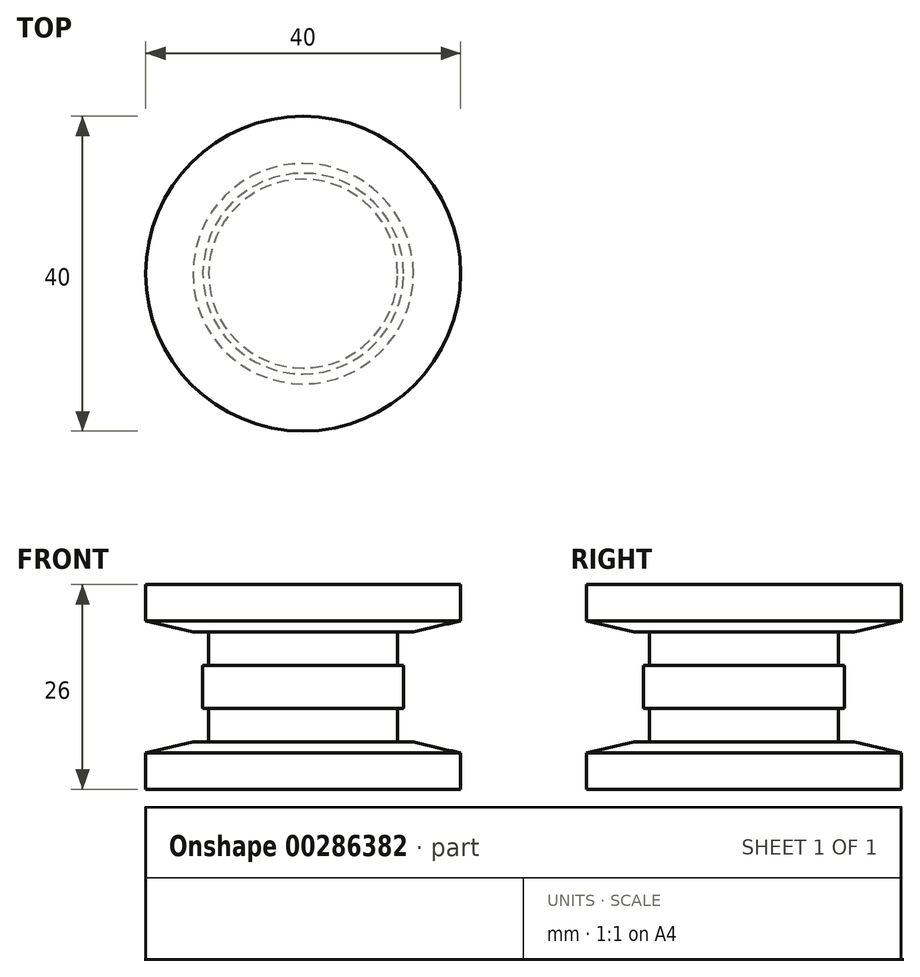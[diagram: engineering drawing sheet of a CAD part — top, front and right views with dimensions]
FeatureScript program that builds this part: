
annotation { "Feature Type Name" : "Feature", "Feature Type Description" : "" }
export const myFeature = defineFeature(function(context is Context, id is Id, definition is map)
    precondition{}
    {
        {
            var Q0;
            Q0=qCreatedBy(makeId("Top.planeOp"),FACE);
            var sketch = newSketch(context, id + "F0", { "sketchPlane" : qUnion([Q0])});
            skCircle(sketch, "E0", {"center": v(0, 0) * mm, "radius": 20 * mm});
            skSolve(sketch);
        }
        {
            var Q0;
            Q0 = qSketchRegion(id + "F0", true);
            extrude(context, id + "F1", {"entities" : qUnion([Q0]), "depth" : 6 * mm});
        }
        {
            var Q0;
            Q0=makeQuery(id+"F1.opExtrude","CAP_FACE",FACE,{"disambiguationData":[OSD([sQuery(id+"F0.wireOp",EDGE,"E0")])],"isStart":false});
            cPlane(context, id + "F2", {"entities" : qUnion([Q0]), "cplaneType" : CPlaneType.OFFSET, "offset" : 0 * mm, "width" : 150 * mm, "height" : 150 * mm});
        }
        {
            var Q0;
            Q0=qCreatedBy(id+"F2.planeOp",FACE);
            var sketch = newSketch(context, id + "F3", { "sketchPlane" : qUnion([Q0])});
            skCircle(sketch, "E1", {"center": v(0, 0) * mm, "radius": 12 * mm});
            skSolve(sketch);
        }
        {
            var Q0;
            Q0 = qSketchRegion(id + "F3", true);
            extrude(context, id + "F4", {"entities" : qUnion([Q0]), "operationType" : NewBodyOperationType.ADD, "depth" : 4.25 * mm});
        }
        {
            var Q0;
            Q0=makeQuery(id+"F4.opExtrude","CAP_FACE",FACE,{"disambiguationData":[OSD([sQuery(id+"F3.wireOp",EDGE,"E1")])],"isStart":false});
            cPlane(context, id + "F5", {"entities" : qUnion([Q0]), "cplaneType" : CPlaneType.OFFSET, "offset" : 0 * mm, "width" : 150 * mm, "height" : 150 * mm});
        }
        {
            var Q0;
            Q0=qCreatedBy(id+"F5.planeOp",FACE);
            var sketch = newSketch(context, id + "F6", { "sketchPlane" : qUnion([Q0])});
            skCircle(sketch, "E2", {"center": v(0, 0) * mm, "radius": 12.75 * mm});
            skSolve(sketch);
        }
        {
            var Q0;
            Q0 = qSketchRegion(id + "F6", true);
            extrude(context, id + "F7", {"entities" : qUnion([Q0]), "operationType" : NewBodyOperationType.ADD, "depth" : 5.5 * mm});
        }
        {
            var Q0;
            Q0=makeQuery(id+"F7.opExtrude","CAP_FACE",FACE,{"disambiguationData":[OSD([sQuery(id+"F6.wireOp",EDGE,"E2")])],"isStart":false});
            cPlane(context, id + "F8", {"entities" : qUnion([Q0]), "cplaneType" : CPlaneType.OFFSET, "offset" : 0 * mm, "width" : 150 * mm, "height" : 150 * mm});
        }
        {
            var Q0;
            Q0=qCreatedBy(id+"F8.planeOp",FACE);
            var sketch = newSketch(context, id + "F9", { "sketchPlane" : qUnion([Q0])});
            skCircle(sketch, "E3", {"center": v(0, 0) * mm, "radius": 12 * mm});
            skSolve(sketch);
        }
        {
            var Q0;
            Q0 = qSketchRegion(id + "F9", true);
            extrude(context, id + "F10", {"entities" : qUnion([Q0]), "operationType" : NewBodyOperationType.ADD, "depth" : 4.25 * mm});
        }
        {
            var Q0;
            Q0=makeQuery(id+"F10.opExtrude","CAP_FACE",FACE,{"disambiguationData":[OSD([sQuery(id+"F9.wireOp",EDGE,"E3")])],"isStart":false});
            cPlane(context, id + "F11", {"entities" : qUnion([Q0]), "cplaneType" : CPlaneType.OFFSET, "offset" : 0 * mm, "width" : 150 * mm, "height" : 150 * mm});
        }
        {
            var Q0;
            Q0=qCreatedBy(id+"F11.planeOp",FACE);
            var sketch = newSketch(context, id + "F12", { "sketchPlane" : qUnion([Q0])});
            skCircle(sketch, "E4", {"center": v(0, 0) * mm, "radius": 20 * mm});
            skSolve(sketch);
        }
        {
            var Q0;
            Q0 = qSketchRegion(id + "F12", true);
            extrude(context, id + "F13", {"entities" : qUnion([Q0]), "operationType" : NewBodyOperationType.ADD, "depth" : 6 * mm});
        }
        {
            var Q0;
            Q0=makeQuery(id+"F1.opExtrude","CAP_EDGE",EDGE,{"disambiguationData":[OSD([sQuery(id+"F0.wireOp",EDGE,"E0")])],"isStart":false});
            chamfer(context, id + "F14", {"entities" : qUnion([Q0]), "chamferType" : ChamferType.TWO_OFFSETS, "width1" : 6 * mm, "oppositeDirection" : false, "width2" : 1.4 * mm, "tangentPropagation" : true});
        }
        {
            var Q0;
            Q0=makeQuery(id+"F13.opExtrude","CAP_EDGE",EDGE,{"disambiguationData":[OSD([sQuery(id+"F12.wireOp",EDGE,"E4")])],"isStart":true});
            chamfer(context, id + "F15", {"entities" : qUnion([Q0]), "chamferType" : ChamferType.TWO_OFFSETS, "width1" : 1.4 * mm, "oppositeDirection" : false, "width2" : 6 * mm, "tangentPropagation" : true});
        }
    });
